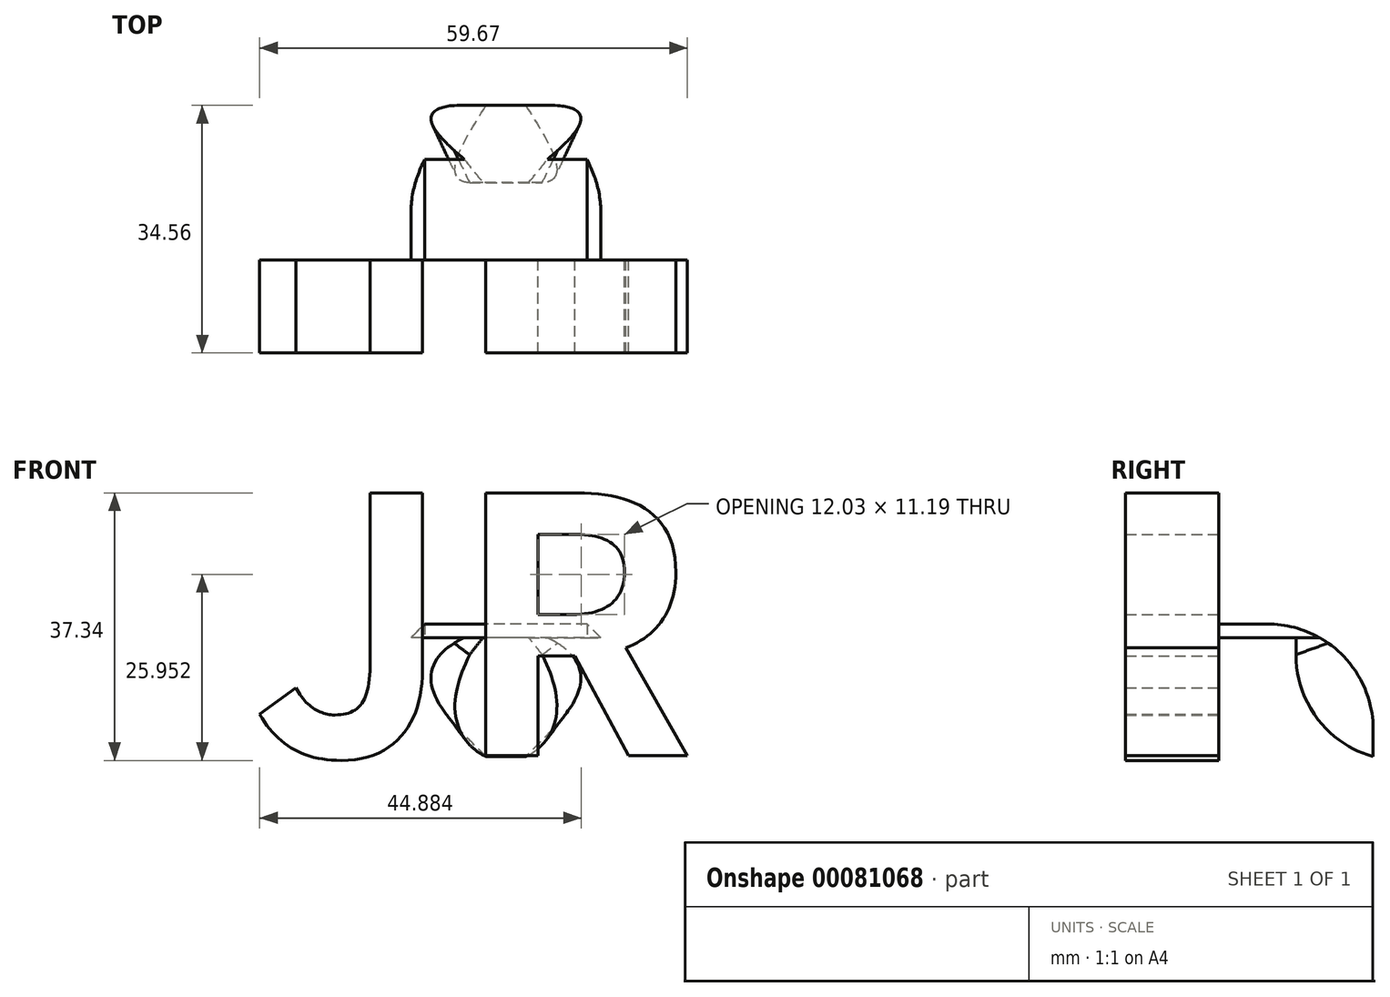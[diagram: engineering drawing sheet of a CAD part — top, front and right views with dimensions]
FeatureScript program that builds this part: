
annotation { "Feature Type Name" : "Feature", "Feature Type Description" : "" }
export const myFeature = defineFeature(function(context is Context, id is Id, definition is map)
    precondition{}
    {
        {
            var Q0;
            Q0=qCreatedBy(makeId("Front.planeOp"),FACE);
            var sketch = newSketch(context, id + "F0", { "sketchPlane" : qUnion([Q0])});
            skText(sketch, "E0", { "text": "JR", "fontName": "NotoSansCJKkr-Bold.otf"});
            const initialGuessF0  = {"E0": [0, -0.03565, 1, 0, 0.03565]};
            skSetInitialGuess(sketch, initialGuessF0);
            skSolve(sketch);
        }
        {
            var Q0;
            Q0 = qSketchRegion(id + "F0", true);
            extrude(context, id + "F1", {"entities" : qUnion([Q0]), "depth" : 13 * mm});
        }
        {
            var Q0;
            Q0=makeQuery(id+"F1.opExtrude","CAP_FACE",FACE,{"disambiguationData":[OSD([sQuery(id+"F0.wireOp",EDGE,"E0.sketch_text.stroke-0"),sQuery(id+"F0.wireOp",EDGE,"E0.sketch_text.stroke-1"),sQuery(id+"F0.wireOp",EDGE,"E0.sketch_text.stroke-2"),sQuery(id+"F0.wireOp",EDGE,"E0.sketch_text.stroke-3"),sQuery(id+"F0.wireOp",EDGE,"E0.sketch_text.stroke-4"),sQuery(id+"F0.wireOp",EDGE,"E0.sketch_text.stroke-5"),sQuery(id+"F0.wireOp",EDGE,"E0.sketch_text.stroke-6"),sQuery(id+"F0.wireOp",EDGE,"E0.sketch_text.stroke-7")])],"isStart":true});
            var sketch = newSketch(context, id + "F2", { "sketchPlane" : qUnion([Q0])});
            skLineSegment(sketch, "E1.bottom", {"start": v(-51.87, -17.31) * mm, "end": v(-19.04, -17.31) * mm});
            skLineSegment(sketch, "E1.top", {"start": v(-51.87, -19.2) * mm, "end": v(-19.04, -19.2) * mm});
            skLineSegment(sketch, "E1.left", {"start": v(-51.87, -17.31) * mm, "end": v(-51.87, -19.2) * mm});
            skLineSegment(sketch, "E1.right", {"start": v(-19.04, -17.31) * mm, "end": v(-19.04, -19.2) * mm});
            skSolve(sketch);
        }
        {
            var Q0;
            Q0 = qSketchRegion(id + "F2", true);
            extrude(context, id + "F3", {"entities" : qUnion([Q0]), "depth" : 21.55 * mm});
        }
        {
            var Q0;
            Q0=makeQuery(id+"F3.opExtrude","SWEPT_FACE",FACE,{"disambiguationData":[OSD([sQuery(id+"F2.wireOp",EDGE,"E1.top")])]});
            var sketch = newSketch(context, id + "F4", { "sketchPlane" : qUnion([Q0])});
            skPoint(sketch, "E2.firstSnap0", {"position": v(51.87, -10.78) * mm});
            skLineSegment(sketch, "E2.bottom", {"start": v(51.87, -10.78) * mm, "end": v(19.04, -10.78) * mm});
            skLineSegment(sketch, "E2.top", {"start": v(51.87, -21.55) * mm, "end": v(19.04, -21.55) * mm});
            skLineSegment(sketch, "E2.left", {"start": v(51.87, -10.78) * mm, "end": v(51.87, -21.55) * mm});
            skLineSegment(sketch, "E2.right", {"start": v(19.04, -10.78) * mm, "end": v(19.04, -21.55) * mm});
            skSolve(sketch);
        }
        {
            var Q0;
            Q0 = qSketchRegion(id + "F4", true);
            extrude(context, id + "F5", {"entities" : qUnion([Q0]), "operationType" : NewBodyOperationType.ADD, "depth" : 16.6 * mm});
        }
        {
            var Q0;
            Q0=makeQuery(id+"F5.opExtrude","CAP_EDGE",EDGE,{"disambiguationData":[OSD([sQuery(id+"F4.wireOp",EDGE,"E2.bottom")])],"isStart":false});
            var Q1;
            Q1=makeQuery(id+"F3.opExtrude","CAP_EDGE",EDGE,{"disambiguationData":[OSD([sQuery(id+"F2.wireOp",EDGE,"E1.bottom")])],"isStart":false});
            fillet(context, id + "F6", {"entities" : qUnion([Q0, Q1]), "radius" : 14.76 * mm, "tangentPropagation" : true, "allowEdgeOverflow" : false});
        }
        {
            var Q0;
            Q0=makeQuery(id+"F6.opFillet","BLEND_EDGE",EDGE,{"blendedFrom":[makeQuery(id+"F3.opExtrude","CAP_EDGE",EDGE,{"disambiguationData":[OSD([sQuery(id+"F2.wireOp",EDGE,"E1.bottom")])],"isStart":false}),makeQuery(id+"F5.boolean.opBoolean","MERGE",FACE,{"derivedFrom":[makeQuery(id+"F3.opExtrude","SWEPT_FACE",FACE,{"disambiguationData":[OSD([sQuery(id+"F2.wireOp",EDGE,"E1.left")])]}),makeQuery(id+"F5.opExtrude","SWEPT_FACE",FACE,{"disambiguationData":[OSD([sQuery(id+"F4.wireOp",EDGE,"E2.left")])]})]})],"blendedInto":[makeQuery(id+"F5.boolean.opBoolean","MERGE",FACE,{"derivedFrom":[makeQuery(id+"F3.opExtrude","SWEPT_FACE",FACE,{"disambiguationData":[OSD([sQuery(id+"F2.wireOp",EDGE,"E1.left")])]}),makeQuery(id+"F5.opExtrude","SWEPT_FACE",FACE,{"disambiguationData":[OSD([sQuery(id+"F4.wireOp",EDGE,"E2.left")])]})]})]});
            var Q1;
            Q1=makeQuery(id+"F6.opFillet","BLEND_EDGE",EDGE,{"blendedFrom":[makeQuery(id+"F3.opExtrude","CAP_EDGE",EDGE,{"disambiguationData":[OSD([sQuery(id+"F2.wireOp",EDGE,"E1.bottom")])],"isStart":false}),makeQuery(id+"F5.boolean.opBoolean","MERGE",FACE,{"derivedFrom":[makeQuery(id+"F3.opExtrude","SWEPT_FACE",FACE,{"disambiguationData":[OSD([sQuery(id+"F2.wireOp",EDGE,"E1.right")])]}),makeQuery(id+"F5.opExtrude","SWEPT_FACE",FACE,{"disambiguationData":[OSD([sQuery(id+"F4.wireOp",EDGE,"E2.right")])]})]})],"blendedInto":[makeQuery(id+"F5.boolean.opBoolean","MERGE",FACE,{"derivedFrom":[makeQuery(id+"F3.opExtrude","SWEPT_FACE",FACE,{"disambiguationData":[OSD([sQuery(id+"F2.wireOp",EDGE,"E1.right")])]}),makeQuery(id+"F5.opExtrude","SWEPT_FACE",FACE,{"disambiguationData":[OSD([sQuery(id+"F4.wireOp",EDGE,"E2.right")])]})]})]});
            chamfer(context, id + "F7", {"entities" : qUnion([Q0, Q1]), "width" : 5.08 * mm, "tangentPropagation" : true});
        }
        {
            var Q0;
            Q0=makeQuery(id+"F7.opChamfer","BLEND_EDGE",EDGE,{"blendedFrom":[makeQuery(id+"F6.opFillet","BLEND_EDGE",EDGE,{"blendedFrom":[makeQuery(id+"F3.opExtrude","CAP_EDGE",EDGE,{"disambiguationData":[OSD([sQuery(id+"F2.wireOp",EDGE,"E1.bottom")])],"isStart":false}),makeQuery(id+"F5.boolean.opBoolean","MERGE",FACE,{"derivedFrom":[makeQuery(id+"F3.opExtrude","SWEPT_FACE",FACE,{"disambiguationData":[OSD([sQuery(id+"F2.wireOp",EDGE,"E1.left")])]}),makeQuery(id+"F5.opExtrude","SWEPT_FACE",FACE,{"disambiguationData":[OSD([sQuery(id+"F4.wireOp",EDGE,"E2.left")])]})]})],"blendedInto":[makeQuery(id+"F5.boolean.opBoolean","MERGE",FACE,{"derivedFrom":[makeQuery(id+"F3.opExtrude","SWEPT_FACE",FACE,{"disambiguationData":[OSD([sQuery(id+"F2.wireOp",EDGE,"E1.left")])]}),makeQuery(id+"F5.opExtrude","SWEPT_FACE",FACE,{"disambiguationData":[OSD([sQuery(id+"F4.wireOp",EDGE,"E2.left")])]})]})]}),makeQuery(id+"F5.opExtrude","SWEPT_FACE",FACE,{"disambiguationData":[OSD([sQuery(id+"F4.wireOp",EDGE,"E2.bottom")])]})],"blendedInto":[makeQuery(id+"F5.opExtrude","SWEPT_FACE",FACE,{"disambiguationData":[OSD([sQuery(id+"F4.wireOp",EDGE,"E2.bottom")])]})]});
            var Q1;
            Q1=makeQuery(id+"F7.opChamfer","BLEND_EDGE",EDGE,{"blendedFrom":[makeQuery(id+"F6.opFillet","BLEND_EDGE",EDGE,{"blendedFrom":[makeQuery(id+"F3.opExtrude","CAP_EDGE",EDGE,{"disambiguationData":[OSD([sQuery(id+"F2.wireOp",EDGE,"E1.bottom")])],"isStart":false}),makeQuery(id+"F5.boolean.opBoolean","MERGE",FACE,{"derivedFrom":[makeQuery(id+"F3.opExtrude","SWEPT_FACE",FACE,{"disambiguationData":[OSD([sQuery(id+"F2.wireOp",EDGE,"E1.right")])]}),makeQuery(id+"F5.opExtrude","SWEPT_FACE",FACE,{"disambiguationData":[OSD([sQuery(id+"F4.wireOp",EDGE,"E2.right")])]})]})],"blendedInto":[makeQuery(id+"F5.boolean.opBoolean","MERGE",FACE,{"derivedFrom":[makeQuery(id+"F3.opExtrude","SWEPT_FACE",FACE,{"disambiguationData":[OSD([sQuery(id+"F2.wireOp",EDGE,"E1.right")])]}),makeQuery(id+"F5.opExtrude","SWEPT_FACE",FACE,{"disambiguationData":[OSD([sQuery(id+"F4.wireOp",EDGE,"E2.right")])]})]})]}),makeQuery(id+"F5.opExtrude","SWEPT_FACE",FACE,{"disambiguationData":[OSD([sQuery(id+"F4.wireOp",EDGE,"E2.bottom")])]})],"blendedInto":[makeQuery(id+"F5.opExtrude","SWEPT_FACE",FACE,{"disambiguationData":[OSD([sQuery(id+"F4.wireOp",EDGE,"E2.bottom")])]})]});
            chamfer(context, id + "F8", {"entities" : qUnion([Q0, Q1]), "width" : 5.08 * mm, "tangentPropagation" : true});
        }
    });
